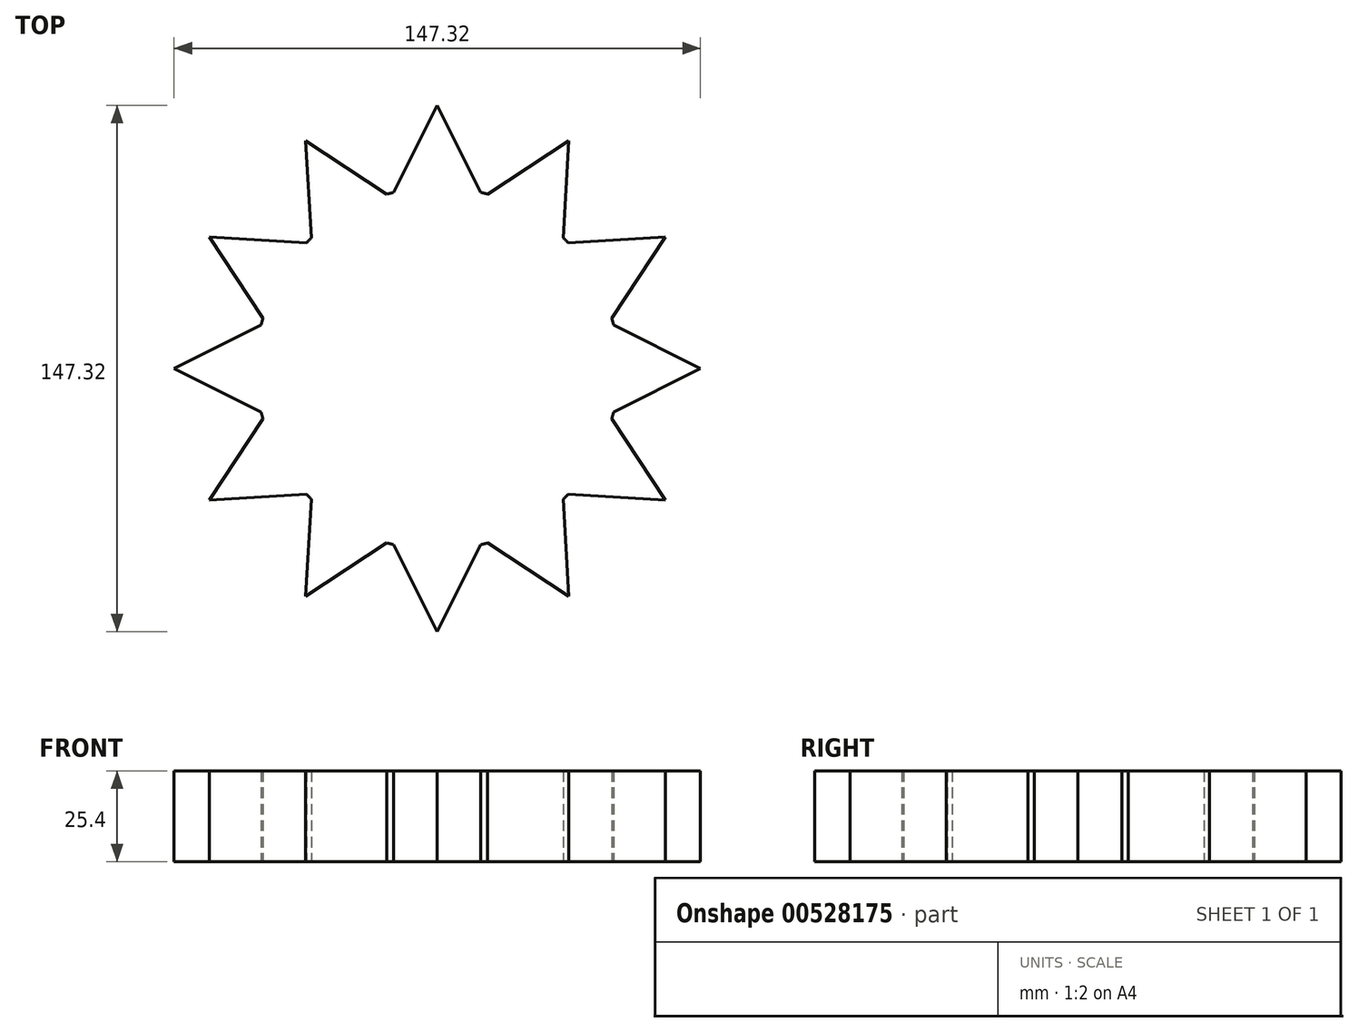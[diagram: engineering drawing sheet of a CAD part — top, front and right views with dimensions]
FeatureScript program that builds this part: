
annotation { "Feature Type Name" : "Feature", "Feature Type Description" : "" }
export const myFeature = defineFeature(function(context is Context, id is Id, definition is map)
    precondition{}
    {
        {
            var Q0;
            Q0=qCreatedBy(makeId("Top.planeOp"),FACE);
            var sketch = newSketch(context, id + "F0", { "sketchPlane" : qUnion([Q0])});
            skCircle(sketch, "E0", {"center": v(0, 0) * mm, "radius": 50.8 * mm});
            skLineSegment(sketch, "E1", {"start": v(0, 0) * mm, "end": v(-100.9, 0) * mm, "construction": true});
            skLineSegment(sketch, "E2", {"start": v(-73.66, 0) * mm, "end": v(-49.31, 12.2) * mm});
            skLineSegment(sketch, "E3.MirrorCS", {"start": v(-73.66, 0) * mm, "end": v(-49.31, -12.2) * mm});
            skLineSegment(sketch, "E4.1.0", {"start": v(-63.8, -36.83) * mm, "end": v(-48.8, -14.1) * mm});
            skLineSegment(sketch, "E4.1.2", {"start": v(-63.8, -36.83) * mm, "end": v(-36.6, -35.22) * mm});
            skLineSegment(sketch, "E4.2.0", {"start": v(-36.83, -63.8) * mm, "end": v(-35.22, -36.6) * mm});
            skLineSegment(sketch, "E4.2.2", {"start": v(-36.83, -63.8) * mm, "end": v(-14.1, -48.8) * mm});
            skLineSegment(sketch, "E4.3.0", {"start": v(0, -73.66) * mm, "end": v(-12.2, -49.31) * mm});
            skLineSegment(sketch, "E4.3.2", {"start": v(0, -73.66) * mm, "end": v(12.2, -49.31) * mm});
            skLineSegment(sketch, "E4.4.0", {"start": v(36.83, -63.8) * mm, "end": v(14.1, -48.8) * mm});
            skLineSegment(sketch, "E4.4.2", {"start": v(36.83, -63.8) * mm, "end": v(35.22, -36.6) * mm});
            skLineSegment(sketch, "E4.5.0", {"start": v(63.8, -36.83) * mm, "end": v(36.6, -35.22) * mm});
            skLineSegment(sketch, "E4.5.2", {"start": v(63.8, -36.83) * mm, "end": v(48.8, -14.1) * mm});
            skLineSegment(sketch, "E4.6.0", {"start": v(73.66, 0) * mm, "end": v(49.31, -12.2) * mm});
            skLineSegment(sketch, "E4.6.2", {"start": v(73.66, 0) * mm, "end": v(49.31, 12.2) * mm});
            skLineSegment(sketch, "E4.7.0", {"start": v(63.8, 36.83) * mm, "end": v(48.8, 14.1) * mm});
            skLineSegment(sketch, "E4.7.2", {"start": v(63.8, 36.83) * mm, "end": v(36.6, 35.22) * mm});
            skLineSegment(sketch, "E4.8.0", {"start": v(36.83, 63.8) * mm, "end": v(35.22, 36.6) * mm});
            skLineSegment(sketch, "E4.8.2", {"start": v(36.83, 63.8) * mm, "end": v(14.1, 48.8) * mm});
            skLineSegment(sketch, "E4.9.0", {"start": v(0, 73.66) * mm, "end": v(12.2, 49.31) * mm});
            skLineSegment(sketch, "E4.9.2", {"start": v(0, 73.66) * mm, "end": v(-12.2, 49.31) * mm});
            skLineSegment(sketch, "E4.10.0", {"start": v(-36.83, 63.8) * mm, "end": v(-14.1, 48.8) * mm});
            skLineSegment(sketch, "E4.10.2", {"start": v(-36.83, 63.8) * mm, "end": v(-35.22, 36.6) * mm});
            skLineSegment(sketch, "E4.11.0", {"start": v(-63.8, 36.83) * mm, "end": v(-36.6, 35.22) * mm});
            skPoint(sketch, "E5.orphan", {"position": v(-29.83, 34.82) * mm});
            skPoint(sketch, "E6.orphan", {"position": v(-43.24, 15.24) * mm});
            skPoint(sketch, "E7.orphan", {"position": v(-45.07, 8.42) * mm});
            skPoint(sketch, "E8.orphan", {"position": v(-15.24, 43.24) * mm});
            skPoint(sketch, "E9.orphan", {"position": v(8.42, 45.07) * mm});
            skPoint(sketch, "E10.orphan", {"position": v(34.82, 29.83) * mm});
            skPoint(sketch, "E11.orphan", {"position": v(29.83, 34.82) * mm});
            skPoint(sketch, "E12.orphan", {"position": v(43.24, 15.24) * mm});
            skPoint(sketch, "E13.orphan", {"position": v(45.07, -8.42) * mm});
            skPoint(sketch, "E14.orphan", {"position": v(43.24, -15.24) * mm});
            skPoint(sketch, "E15.orphan", {"position": v(34.82, -29.83) * mm});
            skPoint(sketch, "E16.orphan", {"position": v(29.83, -34.82) * mm});
            skPoint(sketch, "E17.orphan", {"position": v(15.24, -43.24) * mm});
            skPoint(sketch, "E18.orphan", {"position": v(-8.42, -45.07) * mm});
            skPoint(sketch, "E19.orphan", {"position": v(-29.83, -34.82) * mm});
            skPoint(sketch, "E20.orphan", {"position": v(-34.82, -29.83) * mm});
            skPoint(sketch, "E21.orphan", {"position": v(-43.24, -15.24) * mm});
            skLineSegment(sketch, "E22", {"start": v(-63.8, 36.83) * mm, "end": v(-48.8, 14.1) * mm});
            skSolve(sketch);
        }
        {
            var Q0;
            Q0 = qSketchRegion(id + "F0", true);
            extrude(context, id + "F1", {"entities" : qUnion([Q0]), "depth" : 25.4 * mm, "offsetDistance" : 25.4 * mm});
        }
    });
